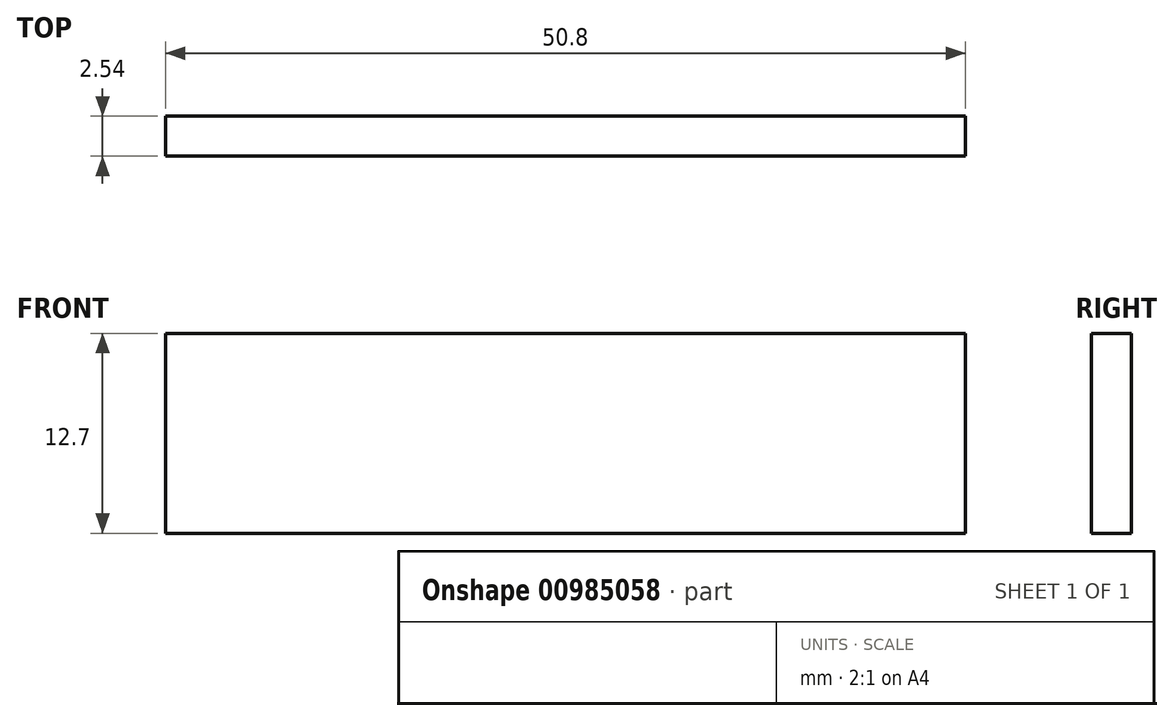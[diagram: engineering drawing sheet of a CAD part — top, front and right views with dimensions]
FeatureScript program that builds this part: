
annotation { "Feature Type Name" : "Feature", "Feature Type Description" : "" }
export const myFeature = defineFeature(function(context is Context, id is Id, definition is map)
    precondition{}
    {
        {
            var Q0;
            Q0=qCreatedBy(makeId("Top.planeOp"),FACE);
            var sketch = newSketch(context, id + "F0", { "sketchPlane" : qUnion([Q0])});
            skLineSegment(sketch, "E0.bottom", {"start": v(25.4, -1.27) * mm, "end": v(-25.4, -1.27) * mm});
            skLineSegment(sketch, "E0.top", {"start": v(25.4, 1.27) * mm, "end": v(-25.4, 1.27) * mm});
            skLineSegment(sketch, "E0.left", {"start": v(25.4, -1.27) * mm, "end": v(25.4, 1.27) * mm});
            skLineSegment(sketch, "E0.right", {"start": v(-25.4, -1.27) * mm, "end": v(-25.4, 1.27) * mm});
            skPoint(sketch, "E0.middle", {"position": v(0, 0) * mm});
            skSolve(sketch);
        }
        {
            var Q0;
            Q0=makeQuery(id+"F0.imprint","IMPRINT",FACE,{"disambiguationData":[TD([[makeQuery(id+"F0.imprint","IMPRINT",EDGE,{"derivedFrom":sQuery(id+"F0.wireOp",EDGE,"E0.bottom")}),-1.0]])]});
            extrude(context, id + "F1", {"entities" : qUnion([Q0]), "depth" : 12.7 * mm, "offsetDistance" : 25.4 * mm});
        }
    });
